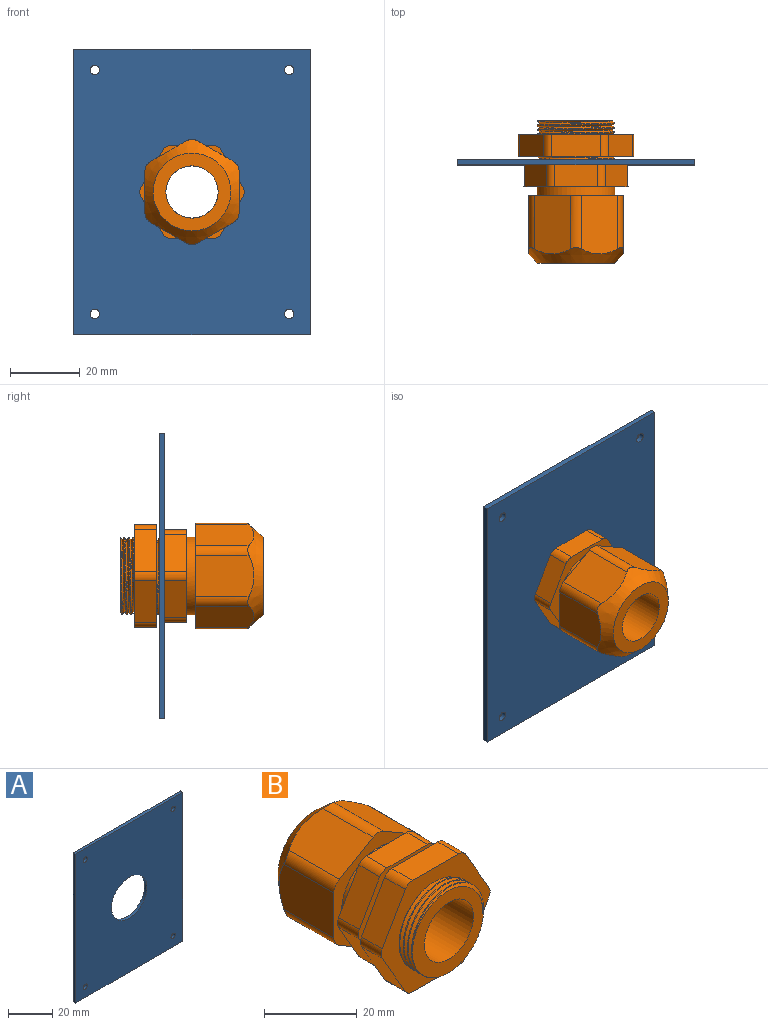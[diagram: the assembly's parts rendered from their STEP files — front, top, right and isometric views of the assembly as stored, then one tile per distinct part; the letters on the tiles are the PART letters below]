
ASSEMBLY  parts=2 mates=1
PART A: 11 faces, bbox 68.1x1.5x82 mm
  f0: plane 68.07x1.52mm, normal (0,0,1), area 103.7mm2, adj f1,f3,f4,f5
  f1: plane 82.04x1.52mm, normal (-1,0,0), area 125mm2, adj f0,f2,f4,f5
  f2: plane 68.07x1.52mm, normal (0,0,-1), area 103.7mm2, adj f1,f3,f4,f5
  f3: plane 82.04x1.52mm, normal (1,0,0), area 125mm2, adj f0,f2,f4,f5
  f4: plane 82.04x68.07mm, normal (0,-1,0), area 5160.4mm2, adj f0,f1,f2,f3,f6,f7,f8,f9
  f5: plane 82.04x68.07mm, normal (0,1,0), area 5160.4mm2, adj f0,f1,f2,f3,f6,f7,f8,f9
  f6: cylinder r=1.35mm len=2.71mm, axis (0,-1,0), area 13mm2, adj f4,f5
  f7: cylinder r=1.35mm len=2.71mm, axis (0,-1,0), area 13mm2, adj f4,f5
  f8: cylinder r=1.35mm len=2.71mm, axis (0,-1,0), area 13mm2, adj f4,f5
  f9: cylinder r=1.35mm len=2.71mm, axis (0,-1,0), area 13mm2, adj f4,f5
  f10: cylinder r=11.3mm len=22.61mm, axis (0,-1,0), area 108.2mm2, adj f4,f5
PART B: 53 faces, bbox 33.9x42.2x30.9 mm
  f0: cylinder r=11.18mm len=22.35mm, axis (0,-1,0), area 60.6mm2, adj f1,f2,f17,f30,f33
  f1: bspline ~25.81x22.37mm, area 82.1mm2, adj f0,f2,f30,f33
  f2: bspline ~25.81x22.35mm, area 109.8mm2, adj f0,f1,f30,f33
  f3: plane 16.75x10.36mm, normal (0.5,0,-0.87), area 194.3mm2, adj f21,f23,f24,f29
  f4: plane 16.75x10.36mm, normal (-0.5,0,-0.87), area 194.3mm2, adj f21,f23,f24,f25
  f5: plane 16.75x11.97mm, normal (-1,0,0), area 194.3mm2, adj f21,f23,f25,f26
  f6: plane 16.75x10.36mm, normal (-0.5,0,0.87), area 194.3mm2, adj f21,f23,f26,f27
  f7: plane 16.75x10.36mm, normal (0.5,0,0.87), area 194.3mm2, adj f21,f23,f27,f28
  f8: plane 16.75x11.97mm, normal (1,0,0), area 194.3mm2, adj f21,f23,f28,f29
  f9: cylinder r=11.18mm len=22.35mm, axis (0,-1,0), area 178.4mm2, adj f16,f21
  f10: plane 10.8x6.35mm, normal (0.87,0,0.5), area 79.2mm2, adj f16,f17,f47,f52
  f11: plane 12.47x6.35mm, normal (0,0,1), area 79.2mm2, adj f16,f17,f47,f48
  f12: plane 10.8x6.35mm, normal (-0.87,0,0.5), area 79.2mm2, adj f16,f17,f48,f49
  f13: plane 10.8x6.35mm, normal (-0.87,0,-0.5), area 79.2mm2, adj f16,f17,f49,f50
  f14: plane 12.47x6.35mm, normal (0,0,-1), area 79.2mm2, adj f16,f17,f50,f51
  f15: plane 10.8x6.35mm, normal (0.87,0,-0.5), area 79.2mm2, adj f16,f17,f51,f52
  f16: plane 30.01x26.67mm, normal (0,1,0), area 221.5mm2, adj f9,f10,f11,f12,f13,f14,f15,f47
  f17: plane 30.01x26.67mm, normal (0,-1,0), area 221.5mm2, adj f0,f10,f11,f12,f13,f14,f15,f47
  f18: plane 22.32x22.31mm, normal (0,-1,0), area 192mm2, adj f19,f22,f31,f32
  f19: cylinder r=11.18mm len=22.35mm, axis (0,-1,0), area 55.3mm2, adj f18,f31,f32,f40
  f20: plane 22.35x22.35mm, normal (0,1,0), area 215.8mm2, adj f22,f23
  f21: plane 30.25x27.05mm, normal (0,-1,0), area 238.1mm2, adj f3,f4,f5,f6,f7,f8,f9,f24
  f22: cylinder r=7.49mm len=41.02mm, axis (0,-1,0), area 1931.3mm2, adj f18,f20
  f23: cone r=11.17mm half-angle=41.2deg, axis (0,-1,0), area 355.2mm2, adj f3,f4,f5,f6,f7,f8,f20,f24
  f24: cylinder r=3.17mm len=15.3mm, axis (0,-1,0), area 50.9mm2, adj f3,f4,f21,f23
  f25: cylinder r=3.17mm len=15.3mm, axis (0,-1,0), area 50.9mm2, adj f4,f5,f21,f23
  f26: cylinder r=3.17mm len=15.3mm, axis (0,-1,0), area 50.9mm2, adj f5,f6,f21,f23
  f27: cylinder r=3.17mm len=15.3mm, axis (0,-1,0), area 50.9mm2, adj f6,f7,f21,f23
  f28: cylinder r=3.17mm len=15.3mm, axis (0,-1,0), area 50.9mm2, adj f7,f8,f21,f23
  f29: cylinder r=3.17mm len=15.3mm, axis (0,-1,0), area 50.9mm2, adj f3,f8,f21,f23
  f30: plane 1.02x0.88mm, normal (0,-0.02,-1), area 0.4mm2, adj f0,f1,f2
  f31: bspline ~22.36x22.32mm, area 219mm2, adj f18,f19,f32,f40
  f32: bspline ~25.81x22.35mm, area 219.4mm2, adj f18,f19,f31,f40
  f33: plane 33.86x30.09mm, normal (0,1,0), area 381.3mm2, adj f0,f1,f2,f34,f35,f36,f37,f38
  f34: plane 12.19x7.04mm, normal (0.87,0,0.5), area 89.4mm2, adj f33,f40,f41,f46
  f35: plane 14.08x6.35mm, normal (0,0,1), area 89.4mm2, adj f33,f40,f41,f42
  f36: plane 12.19x7.04mm, normal (-0.87,0,0.5), area 89.4mm2, adj f33,f40,f42,f43
  f37: plane 12.19x7.04mm, normal (-0.87,0,-0.5), area 89.4mm2, adj f33,f40,f43,f44
  f38: plane 14.08x6.35mm, normal (0,0,-1), area 89.4mm2, adj f33,f40,f44,f45
  f39: plane 12.19x7.04mm, normal (0.87,0,-0.5), area 89.4mm2, adj f33,f40,f45,f46
  f40: plane 33.86x30.09mm, normal (0,-1,0), area 381.4mm2, adj f19,f31,f32,f34,f35,f36,f37,f38
  f41: cylinder r=2.54mm len=6.35mm, axis (0,1,0), area 16.9mm2, adj f33,f34,f35,f40
  f42: cylinder r=2.54mm len=6.35mm, axis (0,1,0), area 16.9mm2, adj f33,f35,f36,f40
  f43: cylinder r=2.54mm len=6.35mm, axis (0,1,0), area 16.9mm2, adj f33,f36,f37,f40
  f44: cylinder r=2.54mm len=6.35mm, axis (0,1,0), area 16.9mm2, adj f33,f37,f38,f40
  f45: cylinder r=2.54mm len=6.35mm, axis (0,1,0), area 16.9mm2, adj f33,f38,f39,f40
  f46: cylinder r=2.54mm len=6.35mm, axis (0,1,0), area 16.9mm2, adj f33,f34,f39,f40
  f47: cylinder r=2.54mm len=6.35mm, axis (0,-1,0), area 16.9mm2, adj f10,f11,f16,f17
  f48: cylinder r=2.54mm len=6.35mm, axis (0,-1,0), area 16.9mm2, adj f11,f12,f16,f17
  f49: cylinder r=2.54mm len=6.35mm, axis (0,-1,0), area 16.9mm2, adj f12,f13,f16,f17
  f50: cylinder r=2.54mm len=6.35mm, axis (0,-1,0), area 16.9mm2, adj f13,f14,f16,f17
  f51: cylinder r=2.54mm len=6.35mm, axis (0,-1,0), area 16.9mm2, adj f14,f15,f16,f17
  f52: cylinder r=2.54mm len=6.35mm, axis (0,-1,0), area 16.9mm2, adj f10,f15,f16,f17
PLACE A t=(0,1.52,82.04)mm
PLACE B rot(axis=(1,0,0),180deg) t=(34.04,12.7,41.02)mm
MATE revolute B.f0 <-> A.f10  axis (0,1,0) through (34.04,0,41.02)mm
